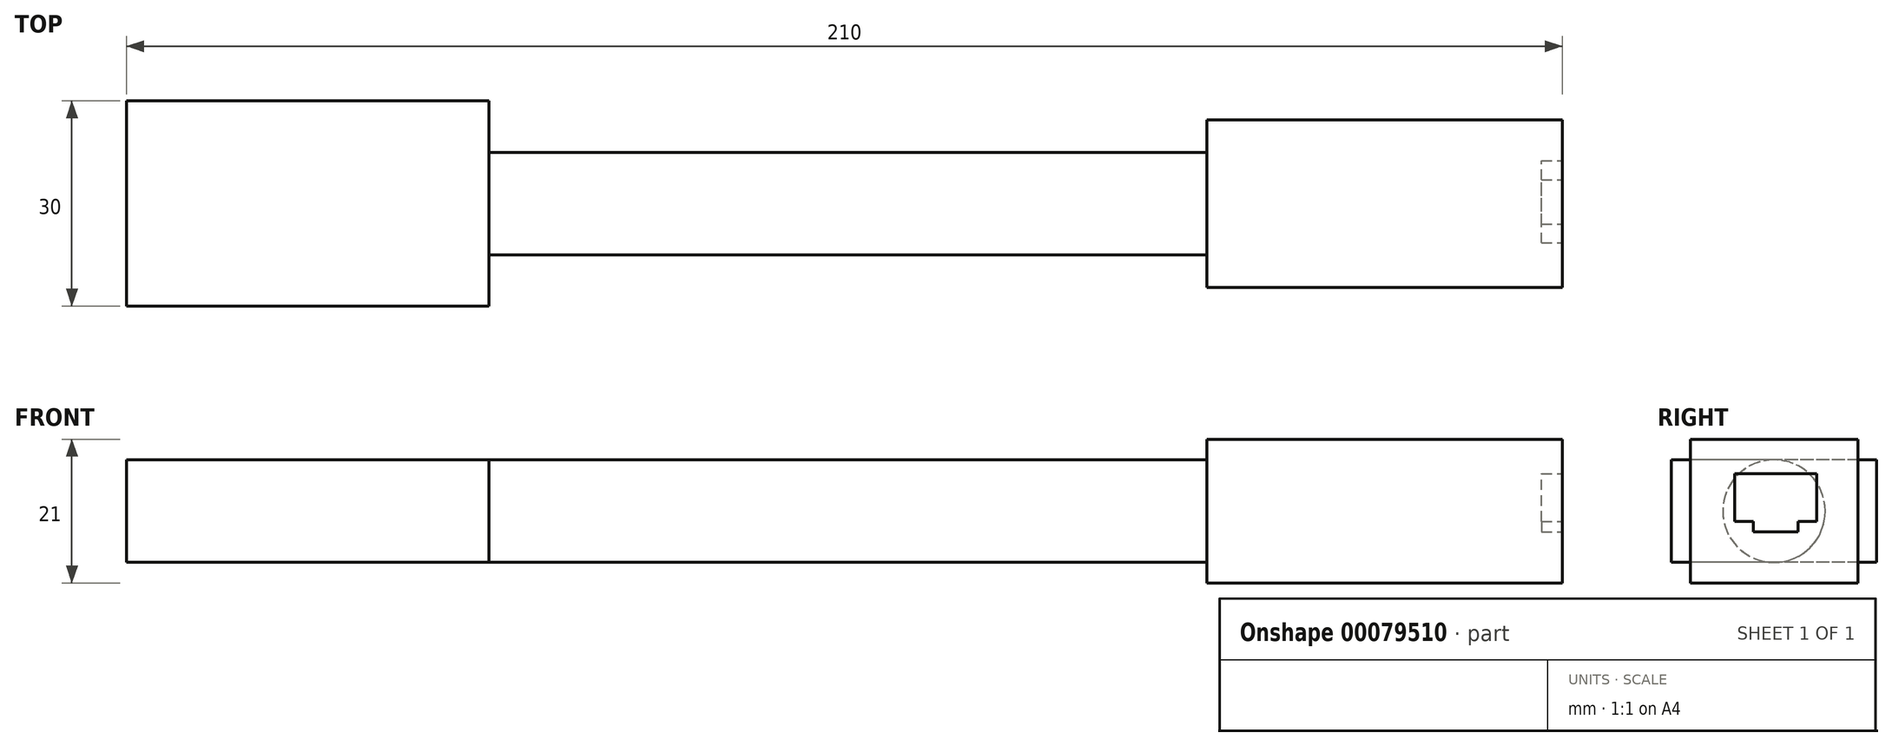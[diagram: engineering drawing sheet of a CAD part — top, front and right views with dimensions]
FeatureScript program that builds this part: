
annotation { "Feature Type Name" : "Feature", "Feature Type Description" : "" }
export const myFeature = defineFeature(function(context is Context, id is Id, definition is map)
    precondition{}
    {
        {
            var Q0;
            Q0=qCreatedBy(makeId("Right.planeOp"),FACE);
            var sketch = newSketch(context, id + "F0", { "sketchPlane" : qUnion([Q0])});
            skLineSegment(sketch, "E0.bottom", {"start": v(-12.25, 10.5) * mm, "end": v(12.25, 10.5) * mm});
            skLineSegment(sketch, "E0.top", {"start": v(-12.25, -10.5) * mm, "end": v(12.25, -10.5) * mm});
            skLineSegment(sketch, "E0.left", {"start": v(-12.25, 10.5) * mm, "end": v(-12.25, -10.5) * mm});
            skLineSegment(sketch, "E0.right", {"start": v(12.25, 10.5) * mm, "end": v(12.25, -10.5) * mm});
            skLineSegment(sketch, "E1", {"start": v(-5.75, -1.5) * mm, "end": v(-5.75, 5.5) * mm});
            skLineSegment(sketch, "E2", {"start": v(-5.75, 5.5) * mm, "end": v(6.25, 5.5) * mm});
            skLineSegment(sketch, "E3", {"start": v(6.25, 5.5) * mm, "end": v(6.25, -1.5) * mm});
            skLineSegment(sketch, "E4", {"start": v(-5.75, -1.5) * mm, "end": v(-3, -1.5) * mm});
            skLineSegment(sketch, "E5", {"start": v(-3, -1.5) * mm, "end": v(-3, -3) * mm});
            skLineSegment(sketch, "E6", {"start": v(-3, -3) * mm, "end": v(3.5, -3) * mm});
            skLineSegment(sketch, "E7", {"start": v(3.5, -3) * mm, "end": v(3.5, -1.5) * mm});
            skLineSegment(sketch, "E8", {"start": v(3.5, -1.5) * mm, "end": v(6.25, -1.5) * mm});
            skSolve(sketch);
        }
        {
            var Q0;
            Q0=makeQuery(id+"F0.imprint","IMPRINT",FACE,{"disambiguationData":[TD([[makeQuery(id+"F0.imprint","IMPRINT",EDGE,{"derivedFrom":sQuery(id+"F0.wireOp",EDGE,"E0.bottom")}),-1.0]])]});
            var Q1;
            Q1=makeQuery(id+"F0.imprint","IMPRINT",FACE,{"disambiguationData":[TD([[makeQuery(id+"F0.imprint","IMPRINT",EDGE,{"derivedFrom":sQuery(id+"F0.wireOp",EDGE,"E1")}),-1.0]])]});
            extrude(context, id + "F1", {"entities" : qUnion([Q0, Q1]), "oppositeDirection" : true, "depth" : 52 * mm});
        }
        {
            var Q0;
            Q0=makeQuery(id+"F1.opExtrude","CAP_FACE",FACE,{"disambiguationData":[OSD([sQuery(id+"F0.wireOp",EDGE,"E0.bottom"),sQuery(id+"F0.wireOp",EDGE,"E0.top"),sQuery(id+"F0.wireOp",EDGE,"E0.left"),sQuery(id+"F0.wireOp",EDGE,"E0.right")])],"isStart":false});
            var sketch = newSketch(context, id + "F2", { "sketchPlane" : qUnion([Q0])});
            skCircle(sketch, "E9", {"center": v(0, 0) * mm, "radius": 7.5 * mm});
            skSolve(sketch);
        }
        {
            var Q0;
            Q0 = qSketchRegion(id + "F2", true);
            extrude(context, id + "F3", {"entities" : qUnion([Q0]), "operationType" : NewBodyOperationType.ADD, "depth" : 105 * mm});
        }
        {
            var Q0;
            Q0=makeQuery(id+"F3.opExtrude","CAP_FACE",FACE,{"disambiguationData":[OSD([sQuery(id+"F2.wireOp",EDGE,"E9")])],"isStart":false});
            var sketch = newSketch(context, id + "F4", { "sketchPlane" : qUnion([Q0])});
            skLineSegment(sketch, "E10.bottom", {"start": v(-15, 7.5) * mm, "end": v(15, 7.5) * mm});
            skLineSegment(sketch, "E10.top", {"start": v(-15, -7.5) * mm, "end": v(15, -7.5) * mm});
            skLineSegment(sketch, "E10.left", {"start": v(-15, 7.5) * mm, "end": v(-15, -7.5) * mm});
            skLineSegment(sketch, "E10.right", {"start": v(15, 7.5) * mm, "end": v(15, -7.5) * mm});
            skSolve(sketch);
        }
        {
            var Q0;
            Q0 = qSketchRegion(id + "F4", true);
            extrude(context, id + "F5", {"entities" : qUnion([Q0]), "operationType" : NewBodyOperationType.ADD, "depth" : 53 * mm});
        }
        {
            var Q0;
            Q0=makeQuery(id+"F0.imprint","IMPRINT",FACE,{"disambiguationData":[TD([[makeQuery(id+"F0.imprint","IMPRINT",EDGE,{"derivedFrom":sQuery(id+"F0.wireOp",EDGE,"E1")}),-1.0]])]});
            extrude(context, id + "F6", {"entities" : qUnion([Q0]), "operationType" : NewBodyOperationType.REMOVE, "oppositeDirection" : true, "depth" : 3 * mm});
        }
    });
